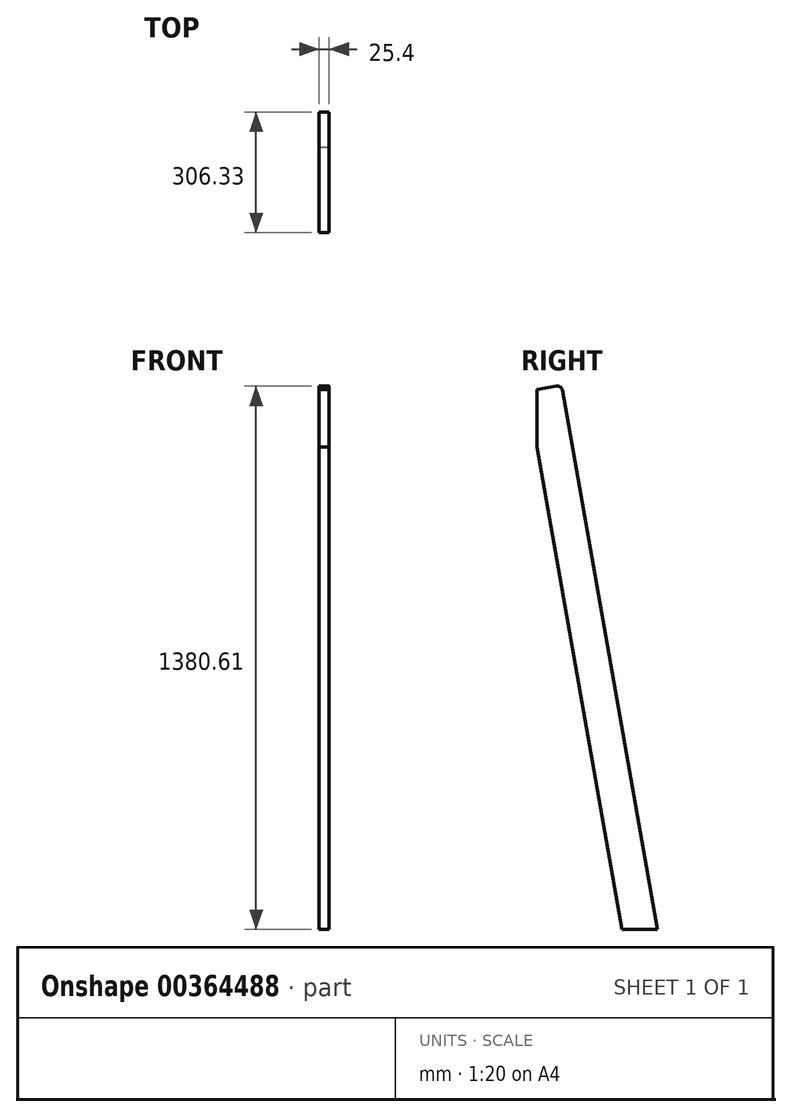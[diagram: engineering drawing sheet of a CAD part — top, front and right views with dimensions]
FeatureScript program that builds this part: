
annotation { "Feature Type Name" : "Feature", "Feature Type Description" : "" }
export const myFeature = defineFeature(function(context is Context, id is Id, definition is map)
    precondition{}
    {
        {
            var Q0;
            Q0=qCreatedBy(makeId("Right.planeOp"),FACE);
            var sketch = newSketch(context, id + "F0", { "sketchPlane" : qUnion([Q0])});
            skLineSegment(sketch, "E0", {"start": v(0, 1225.33) * mm, "end": v(216.06, 0) * mm});
            skLineSegment(sketch, "E1", {"start": v(64.74, 1370.12) * mm, "end": v(306.33, 0) * mm});
            skLineSegment(sketch, "E2", {"start": v(216.06, 0) * mm, "end": v(306.33, 0) * mm});
            skLineSegment(sketch, "E3", {"start": v(0, 1371.6) * mm, "end": v(50.03, 1380.42) * mm});
            skLineSegment(sketch, "E4", {"start": v(0, 1371.6) * mm, "end": v(0, 1225.33) * mm});
            skPoint(sketch, "E5.visualSharp", {"position": v(62.54, 1382.63) * mm});
            skArc(sketch, "E5.filletArc", {"start": v(64.74, 1370.12) * mm, "mid": v(59.52, 1378.32) * mm, "end": v(50.03, 1380.42) * mm});
            skSolve(sketch);
        }
        {
            var Q0;
            Q0=qSketchRegion(id+"F0",true);
            extrude(context, id + "F1", {"entities" : qUnion([Q0]), "depth" : 25.4 * mm});
        }
    });
